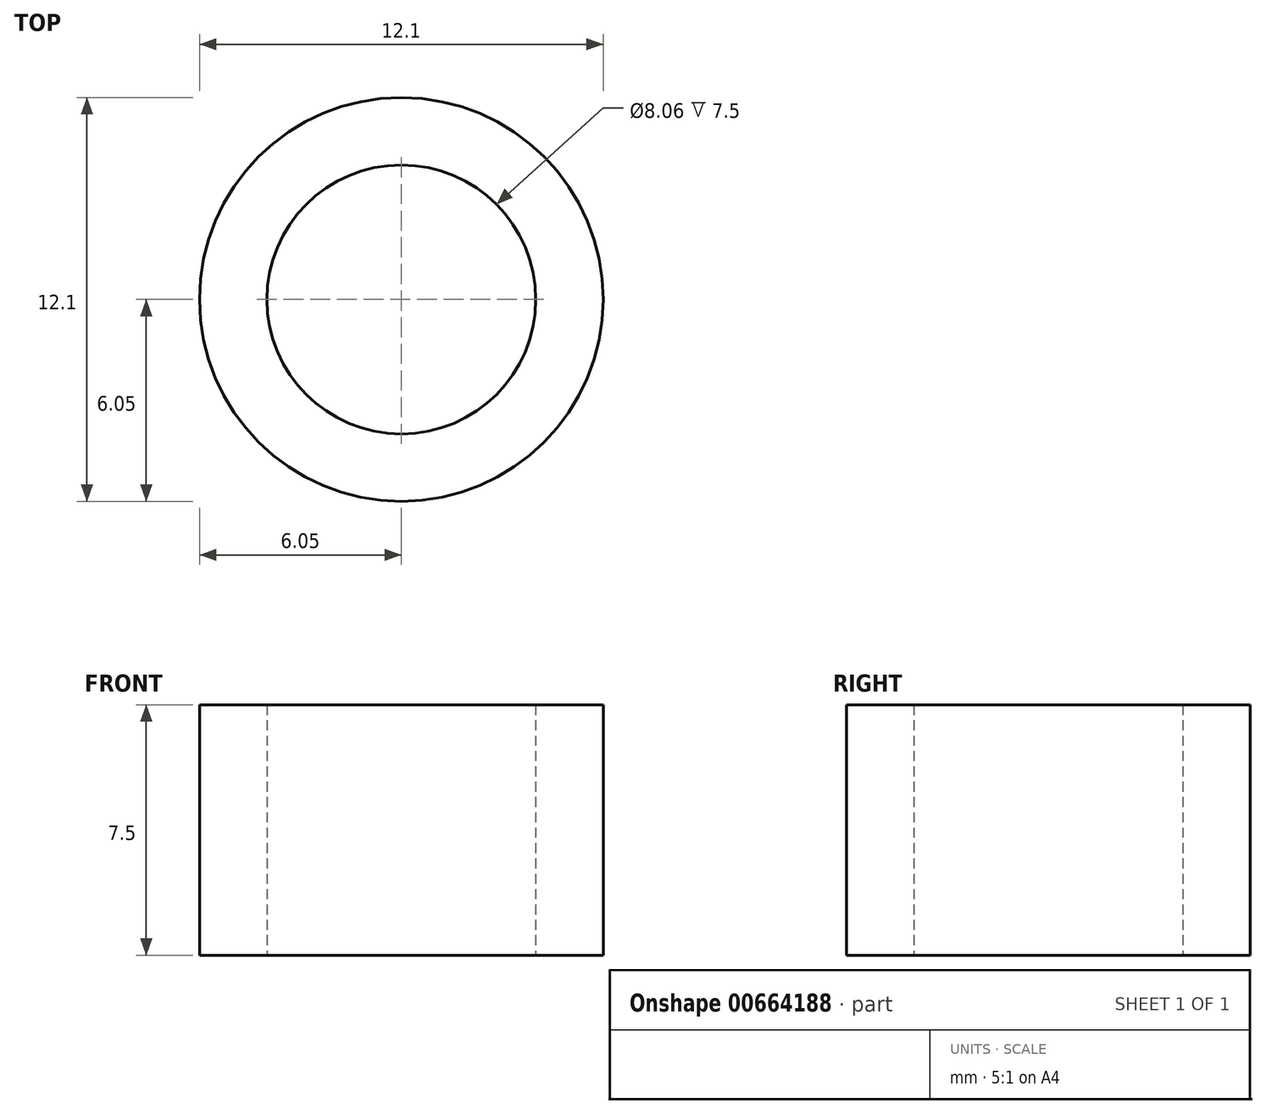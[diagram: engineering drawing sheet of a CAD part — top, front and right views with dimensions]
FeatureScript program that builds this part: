
annotation { "Feature Type Name" : "Feature", "Feature Type Description" : "" }
export const myFeature = defineFeature(function(context is Context, id is Id, definition is map)
    precondition{}
    {
        {
            var Q0;
            Q0=qCreatedBy(makeId("Top.planeOp"),FACE);
            var sketch = newSketch(context, id + "F0", { "sketchPlane" : qUnion([Q0])});
            skCircle(sketch, "E0", {"center": v(0, 0) * mm, "radius": 6.05 * mm});
            skCircle(sketch, "E1", {"center": v(0, 0) * mm, "radius": 4.03 * mm});
            skSolve(sketch);
        }
        {
            var Q0;
            Q0=makeQuery(id+"F0.imprint","IMPRINT",FACE,{"disambiguationData":[TD([[makeQuery(id+"F0.imprint","IMPRINT",EDGE,{"derivedFrom":sQuery(id+"F0.wireOp",EDGE,"E0")}),1.0]])]});
            extrude(context, id + "F1", {"entities" : qUnion([Q0]), "depth" : 7.5 * mm, "offsetDistance" : 25 * mm});
        }
    });
